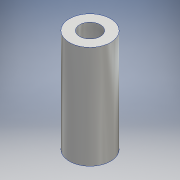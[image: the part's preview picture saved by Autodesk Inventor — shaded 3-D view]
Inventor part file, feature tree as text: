
AUTODESK INVENTOR PART (.ipt)
format: ipt  version: 2020.2 (Build 242310000, 310)  size: 96,256 bytes
history: native  units: mm
features: other x1, extrude x1, sketch x1
ambient origin geometry x8: Origin, YZ Plane, XZ Plane, XY Plane, X Axis, Y Axis, Z Axis, Center Point
bodies: Body1 (feature_tree)
feature tree (3):
  other  "ソリッド1"
  extrude  "押し出し1"  Depth=6.0mm
  sketch  "スケッチ1"
